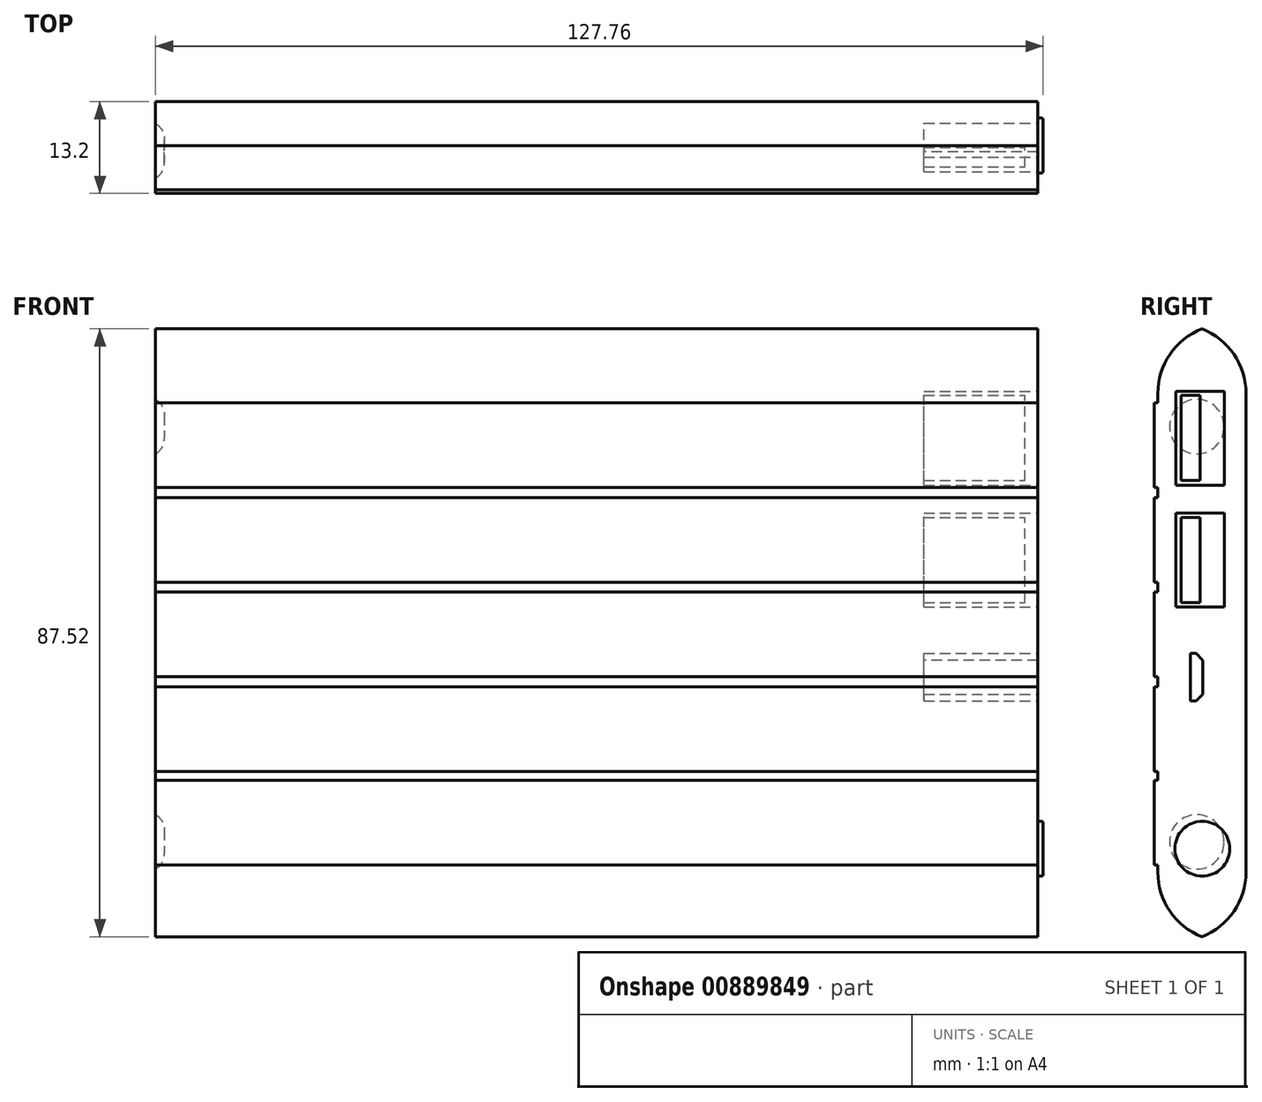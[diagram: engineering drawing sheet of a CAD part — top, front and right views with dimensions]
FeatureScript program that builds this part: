
annotation { "Feature Type Name" : "Feature", "Feature Type Description" : "" }
export const myFeature = defineFeature(function(context is Context, id is Id, definition is map)
    precondition{}
    {
        {
            var Q0;
            Q0=qCreatedBy(makeId("Front.planeOp"),FACE);
            var sketch = newSketch(context, id + "F0", { "sketchPlane" : qUnion([Q0])});
            skLineSegment(sketch, "E0.bottom", {"start": v(-63.5, 44.45) * mm, "end": v(63.5, 44.45) * mm});
            skLineSegment(sketch, "E0.top", {"start": v(-63.5, -44.45) * mm, "end": v(63.5, -44.45) * mm});
            skLineSegment(sketch, "E0.left", {"start": v(-63.5, 44.45) * mm, "end": v(-63.5, -44.45) * mm});
            skLineSegment(sketch, "E0.right", {"start": v(63.5, 44.45) * mm, "end": v(63.5, -44.45) * mm});
            skPoint(sketch, "E0.middle", {"position": v(0, 0) * mm});
            skSolve(sketch);
        }
        {
            var Q0;
            Q0 = qSketchRegion(id + "F0", true);
            extrude(context, id + "F1", {"entities" : qUnion([Q0]), "depth" : 12.7 * mm, "offsetDistance" : 25.4 * mm});
        }
        {
            var Q0;
            Q0=makeQuery(id+"F1.opExtrude","CAP_EDGE",EDGE,{"disambiguationData":[OSD([sQuery(id+"F0.wireOp",EDGE,"E0.bottom")])],"isStart":false});
            var Q1;
            Q1=makeQuery(id+"F1.opExtrude","CAP_EDGE",EDGE,{"disambiguationData":[OSD([sQuery(id+"F0.wireOp",EDGE,"E0.bottom")])],"isStart":true});
            var Q2;
            Q2=makeQuery(id+"F1.opExtrude","CAP_EDGE",EDGE,{"disambiguationData":[OSD([sQuery(id+"F0.wireOp",EDGE,"E0.top")])],"isStart":false});
            var Q3;
            Q3=makeQuery(id+"F1.opExtrude","CAP_EDGE",EDGE,{"disambiguationData":[OSD([sQuery(id+"F0.wireOp",EDGE,"E0.top")])],"isStart":true});
            fillet(context, id + "F2", {"entities" : qUnion([Q0, Q1, Q2, Q3]), "radius" : 10 * mm, "tangentPropagation" : true, "allowEdgeOverflow" : false});
        }
        {
            var Q0;
            Q0=makeQuery(id+"F1.opExtrude","SWEPT_FACE",FACE,{"disambiguationData":[OSD([sQuery(id+"F0.wireOp",EDGE,"E0.right")])]});
            var sketch = newSketch(context, id + "F3", { "sketchPlane" : qUnion([Q0])});
            skLineSegment(sketch, "E1.bottom", {"start": v(-10.1, 21.27) * mm, "end": v(-3.1, 21.27) * mm});
            skLineSegment(sketch, "E1.top", {"start": v(-10.1, 34.77) * mm, "end": v(-3.1, 34.77) * mm});
            skLineSegment(sketch, "E1.left", {"start": v(-10.1, 21.27) * mm, "end": v(-10.1, 34.77) * mm});
            skLineSegment(sketch, "E1.right", {"start": v(-3.1, 21.27) * mm, "end": v(-3.1, 34.77) * mm});
            skPoint(sketch, "E1.middle", {"position": v(-6.6, 28.7) * mm});
            skLineSegment(sketch, "E2.bottom", {"start": v(-10.1, 3.73) * mm, "end": v(-3.1, 3.73) * mm});
            skLineSegment(sketch, "E2.top", {"start": v(-10.1, 17.23) * mm, "end": v(-3.1, 17.23) * mm});
            skLineSegment(sketch, "E2.left", {"start": v(-10.1, 3.73) * mm, "end": v(-10.1, 17.23) * mm});
            skLineSegment(sketch, "E2.right", {"start": v(-3.1, 3.73) * mm, "end": v(-3.1, 17.23) * mm});
            skLineSegment(sketch, "E3.bottom", {"start": v(-8, -9.83) * mm, "end": v(-6.2, -9.83) * mm});
            skLineSegment(sketch, "E3.top", {"start": v(-8, -2.98) * mm, "end": v(-6.2, -2.98) * mm});
            skLineSegment(sketch, "E3.left", {"start": v(-8, -9.83) * mm, "end": v(-8, -2.98) * mm});
            skLineSegment(sketch, "E3.right", {"start": v(-6.2, -9.83) * mm, "end": v(-6.2, -2.98) * mm});
            skPoint(sketch, "E3.middle", {"position": v(-8, -6.4) * mm});
            skPoint(sketch, "E4.oppositeSnap0", {"position": v(-6.6, 17.23) * mm});
            skLineSegment(sketch, "E4.bottom", {"start": v(-9.34, 4.33) * mm, "end": v(-6.6, 4.33) * mm});
            skLineSegment(sketch, "E4.top", {"start": v(-9.34, 16.62) * mm, "end": v(-6.6, 16.62) * mm});
            skLineSegment(sketch, "E4.left", {"start": v(-9.34, 4.33) * mm, "end": v(-9.34, 16.62) * mm});
            skLineSegment(sketch, "E4.right", {"start": v(-6.6, 4.33) * mm, "end": v(-6.6, 16.62) * mm});
            skLineSegment(sketch, "E5.bottom", {"start": v(-9.34, 21.93) * mm, "end": v(-6.6, 21.93) * mm});
            skLineSegment(sketch, "E5.top", {"start": v(-9.34, 34.22) * mm, "end": v(-6.6, 34.22) * mm});
            skLineSegment(sketch, "E5.left", {"start": v(-9.34, 21.93) * mm, "end": v(-9.34, 34.22) * mm});
            skLineSegment(sketch, "E5.right", {"start": v(-6.6, 21.93) * mm, "end": v(-6.6, 34.22) * mm});
            skCircle(sketch, "E6", {"center": v(-6.3, -31.1) * mm, "radius": 3.95 * mm});
            skSolve(sketch);
        }
        {
            var Q0;
            Q0=makeQuery(id+"F3.imprint","IMPRINT",FACE,{"disambiguationData":[TD([[makeQuery(id+"F3.imprint","IMPRINT",EDGE,{"derivedFrom":sQuery(id+"F3.wireOp",EDGE,"E3.bottom")}),1.0]])]});
            var Q1;
            Q1=sQuery(id+"F3.wireOp",EDGE,"E3.left");
            var Q2;
            Q2=sQuery(id+"F3.wireOp",EDGE,"E3.bottom");
            var Q3;
            Q3=sQuery(id+"F3.wireOp",EDGE,"E3.right");
            var Q4;
            Q4=sQuery(id+"F3.wireOp",EDGE,"E3.top");
            extrude(context, id + "F4", {"entities" : qUnion([Q0]), "operationType" : NewBodyOperationType.REMOVE, "surfaceEntities" : qUnion([Q1, Q2, Q3, Q4]), "oppositeDirection" : true, "depth" : 16.4 * mm, "offsetDistance" : 25.4 * mm});
        }
        {
            var Q0;
            Q0=makeQuery(id+"F3.imprint","IMPRINT",FACE,{"disambiguationData":[TD([[makeQuery(id+"F3.imprint","IMPRINT",EDGE,{"derivedFrom":sQuery(id+"F3.wireOp",EDGE,"E2.bottom")}),1.0]])]});
            var Q1;
            Q1=makeQuery(id+"F3.imprint","IMPRINT",FACE,{"disambiguationData":[TD([[makeQuery(id+"F3.imprint","IMPRINT",EDGE,{"derivedFrom":sQuery(id+"F3.wireOp",EDGE,"E1.bottom")}),1.0]])]});
            var Q2;
            Q2=sQuery(id+"F3.wireOp",EDGE,"E2.left");
            var Q3;
            Q3=sQuery(id+"F3.wireOp",EDGE,"E2.top");
            var Q4;
            Q4=sQuery(id+"F3.wireOp",EDGE,"E2.right");
            var Q5;
            Q5=sQuery(id+"F3.wireOp",EDGE,"E2.bottom");
            var Q6;
            Q6=sQuery(id+"F3.wireOp",EDGE,"E1.bottom");
            var Q7;
            Q7=sQuery(id+"F3.wireOp",EDGE,"E1.left");
            var Q8;
            Q8=sQuery(id+"F3.wireOp",EDGE,"E1.right");
            var Q9;
            Q9=sQuery(id+"F3.wireOp",EDGE,"E1.top");
            extrude(context, id + "F5", {"entities" : qUnion([Q0, Q1]), "operationType" : NewBodyOperationType.REMOVE, "surfaceEntities" : qUnion([Q2, Q3, Q4, Q5, Q6, Q7, Q8, Q9]), "oppositeDirection" : true, "depth" : 16.4 * mm, "offsetDistance" : 25.4 * mm});
        }
        {
            var Q0;
            Q0=makeQuery(id+"F4.boolean.opBoolean","COPY",EDGE,{"derivedFrom":makeQuery(id+"F4.opExtrude","SWEPT_EDGE",EDGE,{"disambiguationData":[OSD([sQuery(id+"F3.wireOp",EDGE,"E3.top"),sQuery(id+"F3.wireOp",EDGE,"E3.right")])]})});
            var Q1;
            Q1=makeQuery(id+"F4.boolean.opBoolean","COPY",EDGE,{"derivedFrom":makeQuery(id+"F4.opExtrude","SWEPT_EDGE",EDGE,{"disambiguationData":[OSD([sQuery(id+"F3.wireOp",EDGE,"E3.bottom"),sQuery(id+"F3.wireOp",EDGE,"E3.right")])]})});
            chamfer(context, id + "F6", {"entities" : qUnion([Q0, Q1]), "width" : 1 * mm, "tangentPropagation" : true});
        }
        {
            var Q0;
            Q0=makeQuery(id+"F5.boolean.opBoolean","SPLIT",FACE,{"disambiguationData":[TD([makeQuery(id+"F5.opExtrude","SWEPT_FACE",FACE,{"disambiguationData":[OSD([sQuery(id+"F3.wireOp",EDGE,"E4.bottom")])]})])],"derivedFrom":makeQuery(id+"F1.opExtrude","SWEPT_FACE",FACE,{"disambiguationData":[OSD([sQuery(id+"F0.wireOp",EDGE,"E0.right")])]})});
            var Q1;
            Q1=makeQuery(id+"F5.boolean.opBoolean","SPLIT",FACE,{"disambiguationData":[TD([makeQuery(id+"F5.opExtrude","SWEPT_FACE",FACE,{"disambiguationData":[OSD([sQuery(id+"F3.wireOp",EDGE,"E5.bottom")])]})])],"derivedFrom":makeQuery(id+"F1.opExtrude","SWEPT_FACE",FACE,{"disambiguationData":[OSD([sQuery(id+"F0.wireOp",EDGE,"E0.right")])]})});
            extrude(context, id + "F7", {"entities" : qUnion([Q0, Q1]), "operationType" : NewBodyOperationType.ADD, "oppositeDirection" : true, "depth" : 2.8 * mm, "offsetDistance" : 25.4 * mm});
        }
        {
            var Q0;
            Q0=makeQuery(id+"F5.boolean.opBoolean","SPLIT",FACE,{"disambiguationData":[TD([makeQuery(id+"F5.opExtrude","SWEPT_FACE",FACE,{"disambiguationData":[OSD([sQuery(id+"F3.wireOp",EDGE,"E4.bottom")])]})])],"derivedFrom":makeQuery(id+"F1.opExtrude","SWEPT_FACE",FACE,{"disambiguationData":[OSD([sQuery(id+"F0.wireOp",EDGE,"E0.right")])]})});
            var Q1;
            Q1=makeQuery(id+"F5.boolean.opBoolean","SPLIT",FACE,{"disambiguationData":[TD([makeQuery(id+"F5.opExtrude","SWEPT_FACE",FACE,{"disambiguationData":[OSD([sQuery(id+"F3.wireOp",EDGE,"E5.bottom")])]})])],"derivedFrom":makeQuery(id+"F1.opExtrude","SWEPT_FACE",FACE,{"disambiguationData":[OSD([sQuery(id+"F0.wireOp",EDGE,"E0.right")])]})});
            extrude(context, id + "F8", {"entities" : qUnion([Q0, Q1]), "operationType" : NewBodyOperationType.REMOVE, "oppositeDirection" : true, "depth" : 1.85 * mm, "offsetDistance" : 25.4 * mm});
        }
        {
            var Q0;
            Q0=makeQuery(id+"F3.imprint","IMPRINT",FACE,{"disambiguationData":[TD([[makeQuery(id+"F3.imprint","IMPRINT",EDGE,{"derivedFrom":sQuery(id+"F3.wireOp",EDGE,"E6")}),1.0]])]});
            var Q1;
            Q1=sQuery(id+"F3.wireOp",EDGE,"E6");
            extrude(context, id + "F9", {"entities" : qUnion([Q0]), "operationType" : NewBodyOperationType.ADD, "surfaceEntities" : qUnion([Q1]), "depth" : 0.76 * mm, "offsetDistance" : 25.4 * mm});
        }
        {
            var Q0;
            Q0=makeQuery(id+"F9.opExtrude","CAP_FACE",FACE,{"disambiguationData":[OSD([sQuery(id+"F3.wireOp",EDGE,"E6")])],"isStart":false});
            fillet(context, id + "F10", {"entities" : qUnion([Q0]), "radius" : 0.25 * mm, "tangentPropagation" : true, "allowEdgeOverflow" : false});
        }
        {
            var Q0;
            Q0=makeQuery(id+"F9.opExtrude","CAP_FACE",FACE,{"disambiguationData":[OSD([sQuery(id+"F3.wireOp",EDGE,"E6")])],"isStart":false});
            var sketch = newSketch(context, id + "F11", { "sketchPlane" : qUnion([Q0])});
            skArc(sketch, "E7", {"start": v(-8.24, -32.8) * mm, "mid": v(-3.71, -31.08) * mm, "end": v(-8.26, -29.4) * mm});
            skLineSegment(sketch, "E8", {"start": v(-6.3, -31.1) * mm, "end": v(-8.67, -31.1) * mm});
            skSolve(sketch);
        }
        {
            var Q0;
            Q0=sQuery(id+"F11.wireOp",EDGE,"E8");
            var Q1;
            Q1=sQuery(id+"F11.wireOp",EDGE,"E7");
            extrude(context, id + "F12", {"bodyType" : ToolBodyType.SURFACE, "surfaceEntities" : qUnion([Q0, Q1]), "oppositeDirection" : true, "depth" : 12.7 * mm, "offsetDistance" : 25.4 * mm});
        }
        {
            var Q0;
            Q0=makeQuery(id+"F1.opExtrude","CAP_FACE",FACE,{"disambiguationData":[OSD([sQuery(id+"F0.wireOp",EDGE,"E0.bottom"),sQuery(id+"F0.wireOp",EDGE,"E0.top"),sQuery(id+"F0.wireOp",EDGE,"E0.left"),sQuery(id+"F0.wireOp",EDGE,"E0.right")])],"isStart":false});
            var sketch = newSketch(context, id + "F13", { "sketchPlane" : qUnion([Q0])});
            skLineSegment(sketch, "E9.bottom", {"start": v(-63.5, 33.13) * mm, "end": v(63.5, 33.13) * mm});
            skLineSegment(sketch, "E9.top", {"start": v(-63.5, 20.94) * mm, "end": v(63.5, 20.94) * mm});
            skLineSegment(sketch, "E9.left", {"start": v(-63.5, 33.13) * mm, "end": v(-63.5, 20.94) * mm});
            skLineSegment(sketch, "E9.right", {"start": v(63.5, 33.13) * mm, "end": v(63.5, 20.94) * mm});
            skLineSegment(sketch, "E10.bottom", {"start": v(-63.5, 19.47) * mm, "end": v(63.5, 19.47) * mm});
            skLineSegment(sketch, "E10.top", {"start": v(-63.5, 7.28) * mm, "end": v(63.5, 7.28) * mm});
            skLineSegment(sketch, "E10.left", {"start": v(-63.5, 19.47) * mm, "end": v(-63.5, 7.28) * mm});
            skLineSegment(sketch, "E10.right", {"start": v(63.5, 19.47) * mm, "end": v(63.5, 7.28) * mm});
            skLineSegment(sketch, "E11.bottom", {"start": v(-63.5, 5.88) * mm, "end": v(63.5, 5.88) * mm});
            skLineSegment(sketch, "E11.top", {"start": v(-63.5, -6.31) * mm, "end": v(63.5, -6.31) * mm});
            skLineSegment(sketch, "E11.left", {"start": v(-63.5, 5.88) * mm, "end": v(-63.5, -6.31) * mm});
            skLineSegment(sketch, "E11.right", {"start": v(63.5, 5.88) * mm, "end": v(63.5, -6.31) * mm});
            skLineSegment(sketch, "E12.bottom", {"start": v(-63.5, -7.77) * mm, "end": v(63.5, -7.77) * mm});
            skLineSegment(sketch, "E12.top", {"start": v(-63.5, -19.96) * mm, "end": v(63.5, -19.96) * mm});
            skLineSegment(sketch, "E12.left", {"start": v(-63.5, -7.77) * mm, "end": v(-63.5, -19.96) * mm});
            skLineSegment(sketch, "E12.right", {"start": v(63.5, -7.77) * mm, "end": v(63.5, -19.96) * mm});
            skLineSegment(sketch, "E13.bottom", {"start": v(-63.5, -21.24) * mm, "end": v(63.5, -21.24) * mm});
            skLineSegment(sketch, "E13.top", {"start": v(-63.5, -33.43) * mm, "end": v(63.5, -33.43) * mm});
            skLineSegment(sketch, "E13.left", {"start": v(-63.5, -21.24) * mm, "end": v(-63.5, -33.43) * mm});
            skLineSegment(sketch, "E13.right", {"start": v(63.5, -21.24) * mm, "end": v(63.5, -33.43) * mm});
            skSolve(sketch);
        }
        {
            var Q0;
            Q0 = qSketchRegion(id + "F13", true);
            extrude(context, id + "F14", {"entities" : qUnion([Q0]), "operationType" : NewBodyOperationType.ADD, "depth" : 0.5 * mm, "offsetDistance" : 25.4 * mm});
        }
        {
            var Q0;
            Q0=makeQuery(id+"F14.boolean.opBoolean","MERGE",FACE,{"derivedFrom":[makeQuery(id+"F1.opExtrude","SWEPT_FACE",FACE,{"disambiguationData":[OSD([sQuery(id+"F0.wireOp",EDGE,"E0.left")])]}),makeQuery(id+"F14.opExtrude","SWEPT_FACE",FACE,{"disambiguationData":[OSD([sQuery(id+"F13.wireOp",EDGE,"E9.left")])]}),makeQuery(id+"F14.opExtrude","SWEPT_FACE",FACE,{"disambiguationData":[OSD([sQuery(id+"F13.wireOp",EDGE,"E10.left")])]}),makeQuery(id+"F14.opExtrude","SWEPT_FACE",FACE,{"disambiguationData":[OSD([sQuery(id+"F13.wireOp",EDGE,"E11.left")])]}),makeQuery(id+"F14.opExtrude","SWEPT_FACE",FACE,{"disambiguationData":[OSD([sQuery(id+"F13.wireOp",EDGE,"E12.left")])]}),makeQuery(id+"F14.opExtrude","SWEPT_FACE",FACE,{"disambiguationData":[OSD([sQuery(id+"F13.wireOp",EDGE,"E13.left")])]})]});
            var sketch = newSketch(context, id + "F15", { "sketchPlane" : qUnion([Q0])});
            skCircle(sketch, "E14", {"center": v(7.08, 29.68) * mm, "radius": 3.92 * mm});
            skCircle(sketch, "E15", {"center": v(7.08, -30.1) * mm, "radius": 3.92 * mm});
            skSolve(sketch);
        }
        {
            var Q0;
            Q0=makeQuery(id+"F15.imprint","IMPRINT",FACE,{"disambiguationData":[TD([[makeQuery(id+"F15.imprint","IMPRINT",EDGE,{"derivedFrom":sQuery(id+"F15.wireOp",EDGE,"E15")}),1.0]])]});
            var Q1;
            Q1=makeQuery(id+"F15.imprint","IMPRINT",FACE,{"disambiguationData":[TD([[makeQuery(id+"F15.imprint","IMPRINT",EDGE,{"derivedFrom":sQuery(id+"F15.wireOp",EDGE,"E14")}),1.0]])]});
            var Q2;
            Q2=sQuery(id+"F15.wireOp",EDGE,"E14");
            var Q3;
            Q3=sQuery(id+"F15.wireOp",EDGE,"E15");
            extrude(context, id + "F16", {"entities" : qUnion([Q0, Q1]), "operationType" : NewBodyOperationType.REMOVE, "surfaceEntities" : qUnion([Q2, Q3]), "oppositeDirection" : true, "depth" : 1.27 * mm, "offsetDistance" : 25.4 * mm});
        }
        {
            var Q0;
            Q0=makeQuery(id+"F16.boolean.opBoolean","COPY",EDGE,{"derivedFrom":makeQuery(id+"F16.opExtrude","CAP_EDGE",EDGE,{"disambiguationData":[OSD([sQuery(id+"F15.wireOp",EDGE,"E15")])],"isStart":false})});
            var Q1;
            Q1=makeQuery(id+"F16.boolean.opBoolean","COPY",FACE,{"derivedFrom":makeQuery(id+"F16.opExtrude","CAP_FACE",FACE,{"disambiguationData":[OSD([sQuery(id+"F15.wireOp",EDGE,"E14")])],"isStart":false})});
            fillet(context, id + "F17", {"entities" : qUnion([Q0, Q1]), "radius" : 2.54 * mm, "tangentPropagation" : true, "allowEdgeOverflow" : false});
        }
    });
